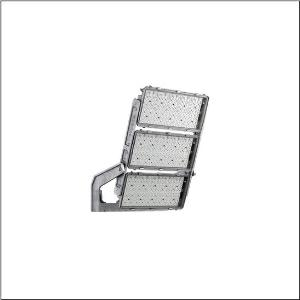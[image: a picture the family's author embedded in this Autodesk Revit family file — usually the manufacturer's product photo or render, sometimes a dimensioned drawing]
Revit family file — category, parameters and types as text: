
# Revit family: floodlight_fl_11_maxi_pro_remote___pl43_5xa779426a01ba_bd65
name_source: partatom
category: Lighting Fixtures
units: mm (PartAtom-declared; Revit-internal decimal feet)

## family parameters
Cut with Voids When Loaded = No
Host = Face
Light Source = No
Part Type = Normal
Room Calculation Point = No
Round Connector Dimension = Use Diameter
Shared = No

## types (1)
- --- (1 x LED, 149370 lm, 1095.8 W, 4000K)
    Apparent Load = 1096 VA
    CIE Flux Codes = 25 74 99 100 100
    Color Rendering = 70
    Color Temperature = 4000K
    Default Elevation = 1800 mm
    Description = Floodlight FL 11  maxi  pro Remote floodlight; light control with lens of PMMA; cover panel of toughened safety glass, transparent; light distribution: PL43, asymmetric direct distribution, LEDcolour temperature: 4000K, rated luminous flux: 149.370lm, colour rendering: CRI > 70, light colour: 740; luminous efficacy: 136lm/W; brightness control: DALI 2 (1 DALI address); with terminal, 8-pole, max. 2.5mm², mains connection: 220..240V/380..400V AC, 50/60Hz, surge voltage resistance: line to ground: 10kV, ECG replaceable separately, no afterglow with DALI off / DMX off command, LED unit replaceable without ESD environment, dustproof LED module, dimming range 10..100%; 1096W floodlight with 2x LED unit of diecast aluminium, coated grey; length: 713mm / width: 651mm / height: 338mm; mounting bracket, of diecast aluminium, uncoated, natural, equipment: Power, protection rating (complete): IP66; insulation class (complete): insulation class I (protective earthing); certification: CE, ENEC, VDE; ball protection: ball impact resistance with accessories, impact resistance: IK07; only for outdoor installations, rated ambient temperature 10°C, permissible operating ambient temperature: -40..+30°C, permissible storage temperature: -40..+85°C; packaging unit: 1 piece

Light Distribution: PL43
    Height = 320 mm
    Lamp = 1 x LED
    Lamp Light Flux = 149370 lm
    Lamp Power = 1095.8 W
    Lamp count = 1
    Length = 1002 mm
    Luminous efficacy = 136 lm/W
    Manufacturer = Siteco
    ModVariant = No
    Model = 5XA779426A01BA
    Mounting Place = Ceiling
    Mounting Type = Surface mounted
    Number of Poles = 1
    OnlyDefault = Yes
    Power Factor = 1
    Product Name = Floodlight FL 11 maxi pro Remote | PL43
    Product group = floodlight | ceiling mounted
    ProductGroupID = 303
    Protection Class = Protection class I
    Protection Degree = IP 66
    RLX_Detail_Level = 1
    RLX_Emergency_Light_Flux = 0 lm
    RLX_Emergency_Type = 0
    RLX_Emergency_Type_DB = No
    RlxData = <blob elided: 52529 chars, md5=cf70fd17>
    Socket = socket
    Standby Power = 0 W
    System Light Flux = 149370 lm
    System Power = 1096 W
    Type Comments = factory setting: luminous flux: 100 % | dim-lin: 254 | 760 mA
    Type Image = l_1006784.jpg
    URL = http://relux.com
    VarID = @adj_044963
    Voltage = 0 V
    Weight = 0.00 kg
    Width = 655 mm

## geometry (parser evidence)
native form markers: Blend x4, Sweep x14
no freeform markers — native parametric forms only
